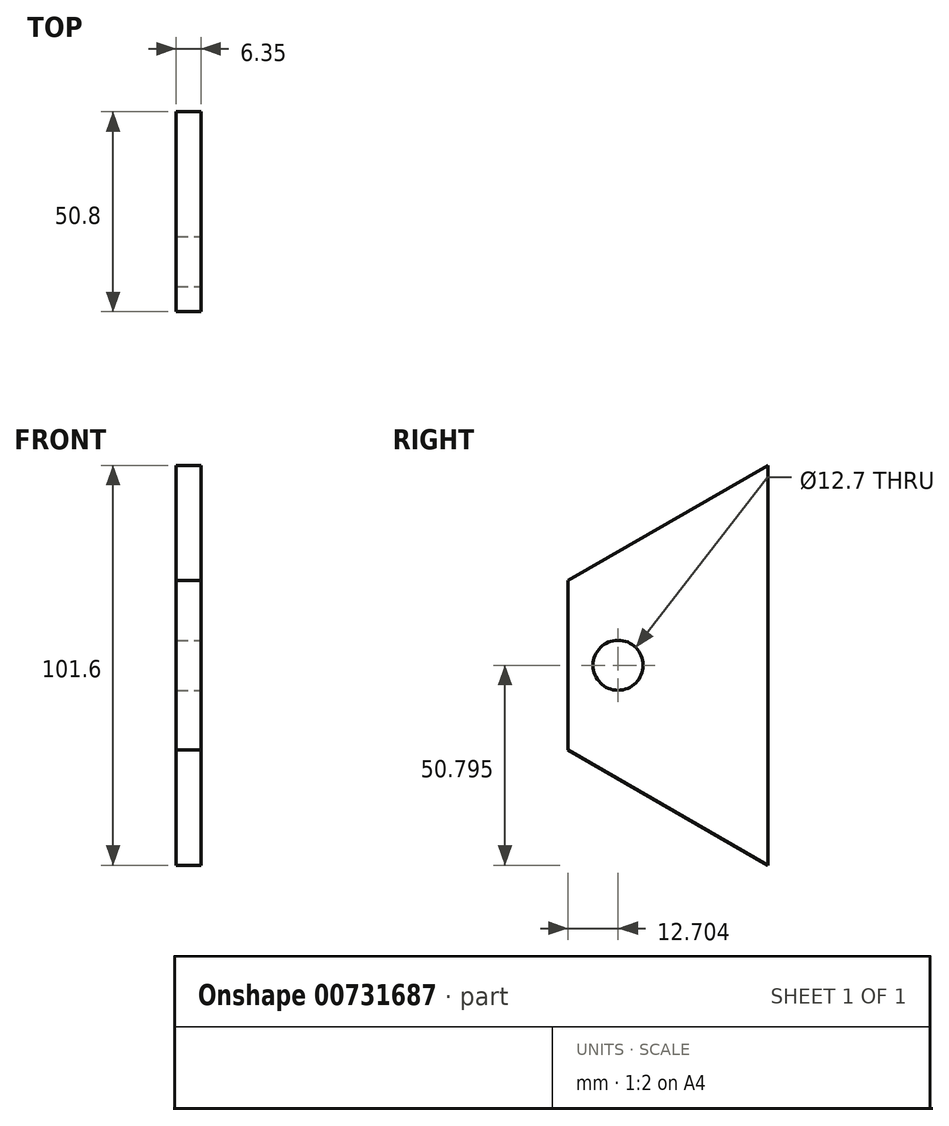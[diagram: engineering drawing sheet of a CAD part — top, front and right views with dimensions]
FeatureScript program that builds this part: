
annotation { "Feature Type Name" : "Feature", "Feature Type Description" : "" }
export const myFeature = defineFeature(function(context is Context, id is Id, definition is map)
    precondition{}
    {
        {
            var Q0;
            Q0=qCreatedBy(makeId("Right.planeOp"),FACE);
            var sketch = newSketch(context, id + "F0", { "sketchPlane" : qUnion([Q0])});
            skLineSegment(sketch, "E0", {"start": v(-73.25, -45.58) * mm, "end": v(-22.45, -74.91) * mm});
            skLineSegment(sketch, "E1", {"start": v(-73.25, -2.64) * mm, "end": v(-22.45, 26.69) * mm});
            skLineSegment(sketch, "E2", {"start": v(-73.25, -2.64) * mm, "end": v(-73.25, -45.58) * mm});
            skLineSegment(sketch, "E3", {"start": v(-22.45, 26.69) * mm, "end": v(-22.45, -74.91) * mm});
            skPoint(sketch, "E4", {"position": v(-60.55, -24.12) * mm});
            skSolve(sketch);
        }
        {
            var Q0;
            Q0=makeQuery(id+"F0.imprint","IMPRINT",FACE,{"disambiguationData":[TD([[makeQuery(id+"F0.imprint","IMPRINT",EDGE,{"derivedFrom":sQuery(id+"F0.wireOp",EDGE,"JDQBFFvR-tl1c-17u7-xjsR-ln2pu06jlJK4")}),1.0]])]});
            var Q1;
            Q1=makeQuery(id+"F0.imprint","IMPRINT",FACE,{"disambiguationData":[TD([[makeQuery(id+"F0.imprint","IMPRINT",EDGE,{"derivedFrom":sQuery(id+"F0.wireOp",EDGE,"E0")}),1.0]])]});
            extrude(context, id + "F1", {"entities" : qUnion([Q0, Q1]), "depth" : 6.35 * mm, "offsetDistance" : 25.4 * mm});
        }
        {
            var Q0;
            Q0=sQuery(id+"F0.wireOp",VERTEX,"E4");
            var Q1;
            Q1=makeQuery(id+"F1.opExtrude","SWEPT_BODY",BODY,{"disambiguationData":[OSD([sQuery(id+"F0.wireOp",EDGE,"E0"),sQuery(id+"F0.wireOp",EDGE,"E1"),sQuery(id+"F0.wireOp",EDGE,"E2"),sQuery(id+"F0.wireOp",EDGE,"E3")])]});
            hole(context, id + "F2", {"style" : HoleStyle.SIMPLE, "endStyle" : HoleEndStyle.THROUGH, "oppositeDirection" : true, "holeDiameter" : 12.7 * mm, "majorDiameter" : 6.35 * mm, "isTappedThrough" : true, "tappedDepth" : 12.7 * mm, "tapClearance" : 3, "locations" : qUnion([Q0]), "scope" : qUnion([Q1]), "startStyle" : HoleStartStyle.SKETCH});
        }
    });
